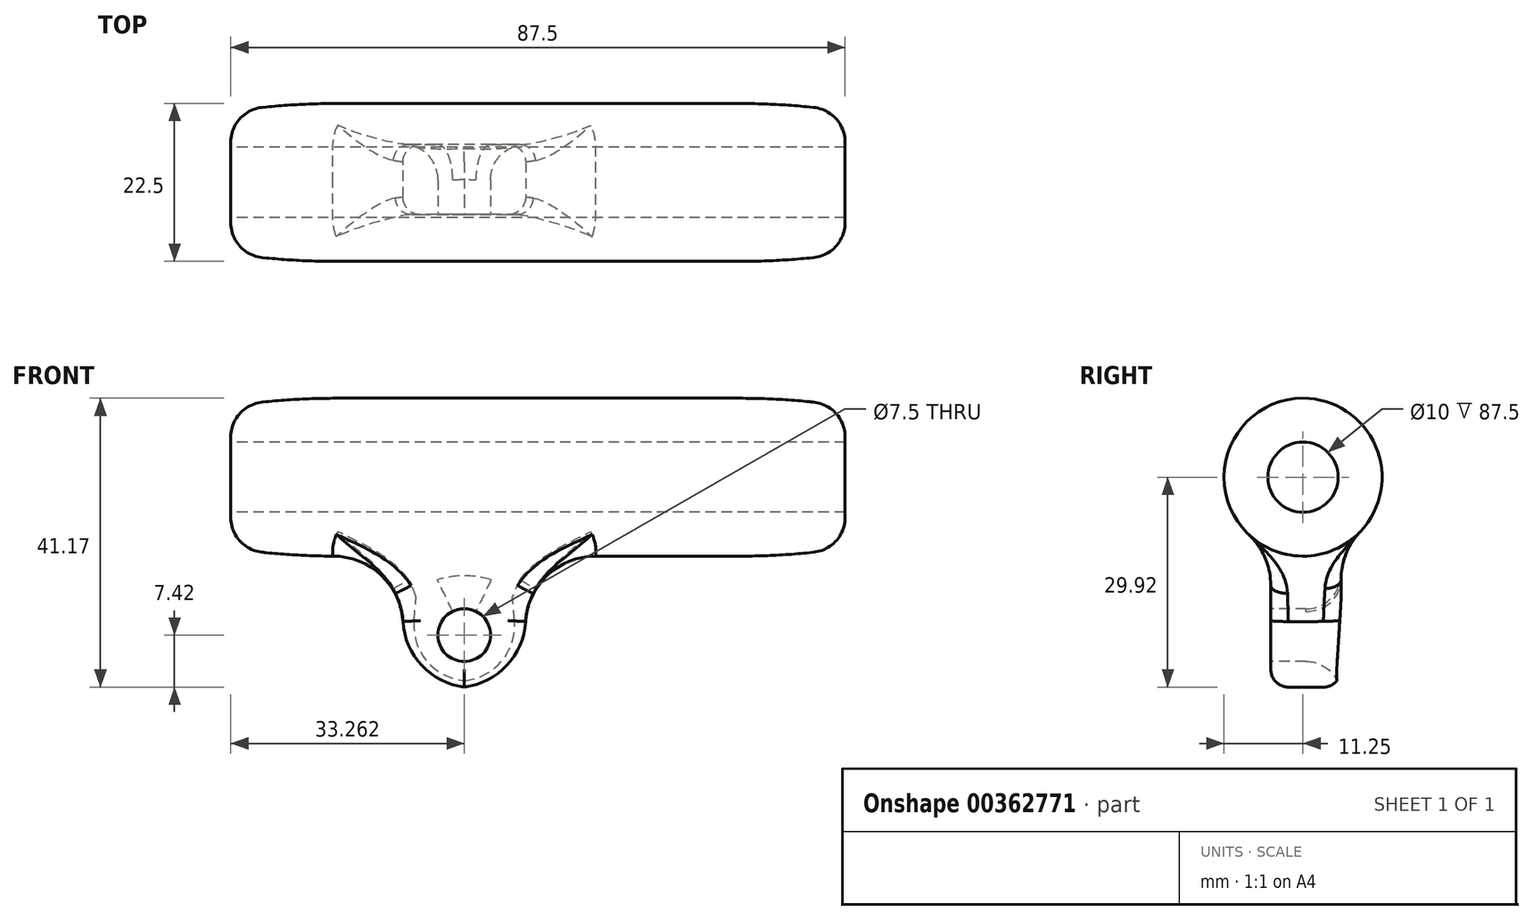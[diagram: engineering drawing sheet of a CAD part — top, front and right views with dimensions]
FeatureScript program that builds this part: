
annotation { "Feature Type Name" : "Feature", "Feature Type Description" : "" }
export const myFeature = defineFeature(function(context is Context, id is Id, definition is map)
    precondition{}
    {
        {
            var Q0;
            Q0=qCreatedBy(makeId("Right.planeOp"),FACE);
            var sketch = newSketch(context, id + "F0", { "sketchPlane" : qUnion([Q0])});
            skCircle(sketch, "E0", {"center": v(0, 0) * mm, "radius": 22.5 * mm});
            skSolve(sketch);
        }
        {
            var Q0;
            Q0=makeQuery(id+"F0.imprint","IMPRINT",FACE,{"disambiguationData":[TD([[makeQuery(id+"F0.imprint","IMPRINT",EDGE,{"derivedFrom":sQuery(id+"F0.wireOp",EDGE,"E0")}),1.0]])]});
            extrude(context, id + "F1", {"entities" : qUnion([Q0]), "depth" : 175 * mm});
        }
        {
            var Q0;
            Q0=qCreatedBy(makeId("Top.planeOp"),FACE);
            var sketch = newSketch(context, id + "F2", { "sketchPlane" : qUnion([Q0])});
            skLineSegment(sketch, "E1.bottom", {"start": v(49.02, -9.18) * mm, "end": v(84.02, -9.18) * mm});
            skLineSegment(sketch, "E1.top", {"start": v(49.02, 10.82) * mm, "end": v(84.02, 10.82) * mm});
            skLineSegment(sketch, "E1.left", {"start": v(49.02, -9.18) * mm, "end": v(49.02, 10.82) * mm});
            skLineSegment(sketch, "E1.right", {"start": v(84.02, -9.18) * mm, "end": v(84.02, 10.82) * mm});
            skSolve(sketch);
        }
        {
            var Q0;
            Q0 = qSketchRegion(id + "F2", true);
            extrude(context, id + "F3", {"entities" : qUnion([Q0]), "operationType" : NewBodyOperationType.ADD, "oppositeDirection" : true, "depth" : 60 * mm});
        }
        {
            var Q0;
            Q0=makeQuery(id+"F1.opExtrude","CAP_FACE",FACE,{"disambiguationData":[OSD([sQuery(id+"F0.wireOp",EDGE,"E0")])],"isStart":true});
            var sketch = newSketch(context, id + "F4", { "sketchPlane" : qUnion([Q0])});
            skCircle(sketch, "E2", {"center": v(0, 0) * mm, "radius": 10 * mm});
            skSolve(sketch);
        }
        {
            var Q0;
            Q0 = qSketchRegion(id + "F4", true);
            extrude(context, id + "F5", {"entities" : qUnion([Q0]), "operationType" : NewBodyOperationType.REMOVE, "endBound" : BoundingType.THROUGH_ALL, "oppositeDirection" : true, "depth" : 25 * mm});
        }
        {
            var Q0;
            Q0=makeQuery(id+"F3.opExtrude","SWEPT_FACE",FACE,{"disambiguationData":[OSD([sQuery(id+"F2.wireOp",EDGE,"E1.bottom")])]});
            var sketch = newSketch(context, id + "F6", { "sketchPlane" : qUnion([Q0])});
            skCircle(sketch, "E3", {"center": v(66.52, -45) * mm, "radius": 7.5 * mm});
            skPoint(sketch, "E3.centerSnap0", {"position": v(66.52, -60) * mm});
            skSolve(sketch);
        }
        {
            var Q0;
            Q0=makeQuery(id+"F6.imprint","IMPRINT",FACE,{"disambiguationData":[TD([[makeQuery(id+"F6.imprint","IMPRINT",EDGE,{"derivedFrom":sQuery(id+"F6.wireOp",EDGE,"E3")}),1.0]])]});
            extrude(context, id + "F7", {"entities" : qUnion([Q0]), "operationType" : NewBodyOperationType.REMOVE, "endBound" : BoundingType.THROUGH_ALL, "oppositeDirection" : true, "depth" : 25 * mm});
        }
        {
            var Q0;
            Q0=makeQuery(id+"F3.opExtrude","CAP_EDGE",EDGE,{"disambiguationData":[OSD([sQuery(id+"F2.wireOp",EDGE,"E1.right")])],"isStart":false});
            var Q1;
            Q1=makeQuery(id+"F3.opExtrude","CAP_EDGE",EDGE,{"disambiguationData":[OSD([sQuery(id+"F2.wireOp",EDGE,"E1.left")])],"isStart":false});
            fillet(context, id + "F8", {"entities" : qUnion([Q0, Q1]), "radius" : 20 * mm, "tangentPropagation" : true, "allowEdgeOverflow" : false});
        }
        {
            var Q0;
            Q0=makeQuery(id+"F3.boolean.opBoolean","INTERSECT",EDGE,{"derivedFrom":[makeQuery(id+"F1.opExtrude","SWEPT_FACE",FACE,{"disambiguationData":[OSD([sQuery(id+"F0.wireOp",EDGE,"E0")])]}),makeQuery(id+"F3.opExtrude","SWEPT_FACE",FACE,{"disambiguationData":[OSD([sQuery(id+"F2.wireOp",EDGE,"E1.right")])]})]});
            fillet(context, id + "F9", {"entities" : qUnion([Q0]), "radius" : 20 * mm, "tangentPropagation" : true, "allowEdgeOverflow" : false});
        }
        {
            var Q0;
            Q0=makeQuery(id+"F3.boolean.opBoolean","INTERSECT",EDGE,{"derivedFrom":[makeQuery(id+"F1.opExtrude","SWEPT_FACE",FACE,{"disambiguationData":[OSD([sQuery(id+"F0.wireOp",EDGE,"E0")])]}),makeQuery(id+"F3.opExtrude","SWEPT_FACE",FACE,{"disambiguationData":[OSD([sQuery(id+"F2.wireOp",EDGE,"E1.left")])]})]});
            fillet(context, id + "F10", {"entities" : qUnion([Q0]), "radius" : 20 * mm, "tangentPropagation" : true, "allowEdgeOverflow" : false});
        }
        {
            var Q0;
            Q0=makeQuery(id+"F3.boolean.opBoolean","INTERSECT",EDGE,{"derivedFrom":[makeQuery(id+"F1.opExtrude","SWEPT_FACE",FACE,{"disambiguationData":[OSD([sQuery(id+"F0.wireOp",EDGE,"E0")])]}),makeQuery(id+"F3.opExtrude","SWEPT_FACE",FACE,{"disambiguationData":[OSD([sQuery(id+"F2.wireOp",EDGE,"E1.top")])]})]});
            var Q1;
            Q1=makeQuery(id+"F3.boolean.opBoolean","INTERSECT",EDGE,{"derivedFrom":[makeQuery(id+"F1.opExtrude","SWEPT_FACE",FACE,{"disambiguationData":[OSD([sQuery(id+"F0.wireOp",EDGE,"E0")])]}),makeQuery(id+"F3.opExtrude","SWEPT_FACE",FACE,{"disambiguationData":[OSD([sQuery(id+"F2.wireOp",EDGE,"E1.bottom")])]})]});
            fillet(context, id + "F11", {"entities" : qUnion([Q0, Q1]), "radius" : 20 * mm, "tangentPropagation" : true, "allowEdgeOverflow" : false});
        }
        {
            var Q0;
            {var subQ0=sQuery(id+"F0.wireOp",EDGE,"E0");Q0=makeQuery(id+"F11.opFillet","BLEND_EDGE",EDGE,{"blendedFrom":[makeQuery(id+"F3.boolean.opBoolean","INTERSECT",EDGE,{"derivedFrom":[makeQuery(id+"F1.opExtrude","SWEPT_FACE",FACE,{"disambiguationData":[OSD([subQ0])]}),makeQuery(id+"F3.opExtrude","SWEPT_FACE",FACE,{"disambiguationData":[OSD([sQuery(id+"F2.wireOp",EDGE,"E1.top")])]})]}),makeQuery(id+"F9.opFillet","BLEND_FACE",FACE,{"disambiguationData":[OSD([subQ0,sQuery(id+"F2.wireOp",EDGE,"E1.right")])]})],"blendedInto":[makeQuery(id+"F9.opFillet","BLEND_FACE",FACE,{"disambiguationData":[OSD([subQ0,sQuery(id+"F2.wireOp",EDGE,"E1.right")])]})]});}
            var Q1;
            {var subQ0=sQuery(id+"F0.wireOp",EDGE,"E0");Q1=makeQuery(id+"F11.opFillet","BLEND_EDGE",EDGE,{"blendedFrom":[makeQuery(id+"F3.boolean.opBoolean","INTERSECT",EDGE,{"derivedFrom":[makeQuery(id+"F1.opExtrude","SWEPT_FACE",FACE,{"disambiguationData":[OSD([subQ0])]}),makeQuery(id+"F3.opExtrude","SWEPT_FACE",FACE,{"disambiguationData":[OSD([sQuery(id+"F2.wireOp",EDGE,"E1.top")])]})]}),makeQuery(id+"F10.opFillet","BLEND_FACE",FACE,{"disambiguationData":[OSD([subQ0,sQuery(id+"F2.wireOp",EDGE,"E1.left")])]})],"blendedInto":[makeQuery(id+"F10.opFillet","BLEND_FACE",FACE,{"disambiguationData":[OSD([subQ0,sQuery(id+"F2.wireOp",EDGE,"E1.left")])]})]});}
            var Q2;
            {var subQ0=sQuery(id+"F0.wireOp",EDGE,"E0");Q2=makeQuery(id+"F11.opFillet","BLEND_EDGE",EDGE,{"blendedFrom":[makeQuery(id+"F3.boolean.opBoolean","INTERSECT",EDGE,{"derivedFrom":[makeQuery(id+"F1.opExtrude","SWEPT_FACE",FACE,{"disambiguationData":[OSD([subQ0])]}),makeQuery(id+"F3.opExtrude","SWEPT_FACE",FACE,{"disambiguationData":[OSD([sQuery(id+"F2.wireOp",EDGE,"E1.bottom")])]})]}),makeQuery(id+"F10.opFillet","BLEND_FACE",FACE,{"disambiguationData":[OSD([subQ0,sQuery(id+"F2.wireOp",EDGE,"E1.left")])]})],"blendedInto":[makeQuery(id+"F10.opFillet","BLEND_FACE",FACE,{"disambiguationData":[OSD([subQ0,sQuery(id+"F2.wireOp",EDGE,"E1.left")])]})]});}
            var Q3;
            {var subQ0=sQuery(id+"F0.wireOp",EDGE,"E0");Q3=makeQuery(id+"F11.opFillet","BLEND_EDGE",EDGE,{"blendedFrom":[makeQuery(id+"F3.boolean.opBoolean","INTERSECT",EDGE,{"derivedFrom":[makeQuery(id+"F1.opExtrude","SWEPT_FACE",FACE,{"disambiguationData":[OSD([subQ0])]}),makeQuery(id+"F3.opExtrude","SWEPT_FACE",FACE,{"disambiguationData":[OSD([sQuery(id+"F2.wireOp",EDGE,"E1.bottom")])]})]}),makeQuery(id+"F9.opFillet","BLEND_FACE",FACE,{"disambiguationData":[OSD([subQ0,sQuery(id+"F2.wireOp",EDGE,"E1.right")])]})],"blendedInto":[makeQuery(id+"F9.opFillet","BLEND_FACE",FACE,{"disambiguationData":[OSD([subQ0,sQuery(id+"F2.wireOp",EDGE,"E1.right")])]})]});}
            fillet(context, id + "F12", {"entities" : qUnion([Q0, Q1, Q2, Q3]), "radius" : 5 * mm, "tangentPropagation" : true, "allowEdgeOverflow" : false});
        }
        {
            var Q0;
            Q0=makeQuery(id+"F1.opExtrude","SWEPT_BODY",BODY,{"disambiguationData":[OSD([sQuery(id+"F0.wireOp",EDGE,"E0")])]});
            var Q1;
            Q1=qCreatedBy(makeId("Origin.pointOp"),VERTEX);
            transform(context, id + "F13", {"entities" : qUnion([Q0]), "transformType" : TransformType.SCALE_UNIFORMLY, "scale" : 0.5, "scalePoint" : qUnion([Q1]), "makeCopy" : false});
        }
        {
            var Q0;
            Q0=makeQuery(id+"F1.opExtrude","CAP_EDGE",EDGE,{"disambiguationData":[OSD([sQuery(id+"F0.wireOp",EDGE,"E0")])],"isStart":false});
            chamfer(context, id + "F14", {"entities" : qUnion([Q0]), "chamferType" : ChamferType.TWO_OFFSETS, "width1" : 1 * mm, "oppositeDirection" : false, "width2" : 10 * mm, "tangentPropagation" : true});
        }
        {
            var Q0;
            Q0=makeQuery(id+"F1.opExtrude","CAP_EDGE",EDGE,{"disambiguationData":[OSD([sQuery(id+"F0.wireOp",EDGE,"E0")])],"isStart":true});
            chamfer(context, id + "F15", {"entities" : qUnion([Q0]), "chamferType" : ChamferType.TWO_OFFSETS, "width1" : 10 * mm, "oppositeDirection" : false, "width2" : 1 * mm, "tangentPropagation" : true});
        }
        {
            var Q0;
            {var subQ0=sQuery(id+"F0.wireOp",EDGE,"E0");Q0=makeQuery(id+"F15.opChamfer","BLEND_EDGE",EDGE,{"blendedFrom":[makeQuery(id+"F1.opExtrude","CAP_EDGE",EDGE,{"disambiguationData":[OSD([subQ0])],"isStart":true}),makeQuery(id+"F1.opExtrude","SWEPT_FACE",FACE,{"disambiguationData":[OSD([subQ0])]})],"blendedInto":[makeQuery(id+"F1.opExtrude","SWEPT_FACE",FACE,{"disambiguationData":[OSD([subQ0])]})]});}
            var Q1;
            {var subQ0=sQuery(id+"F0.wireOp",EDGE,"E0");Q1=makeQuery(id+"F14.opChamfer","BLEND_EDGE",EDGE,{"blendedFrom":[makeQuery(id+"F1.opExtrude","CAP_EDGE",EDGE,{"disambiguationData":[OSD([subQ0])],"isStart":false}),makeQuery(id+"F1.opExtrude","SWEPT_FACE",FACE,{"disambiguationData":[OSD([subQ0])]})],"blendedInto":[makeQuery(id+"F1.opExtrude","SWEPT_FACE",FACE,{"disambiguationData":[OSD([subQ0])]})]});}
            fillet(context, id + "F16", {"entities" : qUnion([Q0, Q1]), "radius" : 100 * mm, "tangentPropagation" : true, "allowEdgeOverflow" : false});
        }
        {
            var Q0;
            {var subQ0=sQuery(id+"F0.wireOp",EDGE,"E0");Q0=makeQuery(id+"F14.opChamfer","BLEND_EDGE",EDGE,{"blendedFrom":[makeQuery(id+"F1.opExtrude","CAP_EDGE",EDGE,{"disambiguationData":[OSD([subQ0])],"isStart":false}),makeQuery(id+"F1.opExtrude","CAP_FACE",FACE,{"disambiguationData":[OSD([subQ0])],"isStart":false})],"blendedInto":[makeQuery(id+"F1.opExtrude","CAP_FACE",FACE,{"disambiguationData":[OSD([subQ0])],"isStart":false})]});}
            var Q1;
            {var subQ0=sQuery(id+"F0.wireOp",EDGE,"E0");Q1=makeQuery(id+"F15.opChamfer","BLEND_EDGE",EDGE,{"blendedFrom":[makeQuery(id+"F1.opExtrude","CAP_EDGE",EDGE,{"disambiguationData":[OSD([subQ0])],"isStart":true}),makeQuery(id+"F1.opExtrude","CAP_FACE",FACE,{"disambiguationData":[OSD([subQ0])],"isStart":true})],"blendedInto":[makeQuery(id+"F1.opExtrude","CAP_FACE",FACE,{"disambiguationData":[OSD([subQ0])],"isStart":true})]});}
            var Q2;
            Q2=makeQuery(id+"F7.boolean.opBoolean","INTERSECT",EDGE,{"derivedFrom":[makeQuery(id+"F3.opExtrude","SWEPT_FACE",FACE,{"disambiguationData":[OSD([sQuery(id+"F2.wireOp",EDGE,"E1.top")])]}),makeQuery(id+"F7.opExtrude","SWEPT_FACE",FACE,{"disambiguationData":[OSD([sQuery(id+"F6.wireOp",EDGE,"E3")])]})]});
            var Q3;
            Q3=makeQuery(id+"F7.boolean.opBoolean","COPY",EDGE,{"derivedFrom":makeQuery(id+"F7.opExtrude","CAP_EDGE",EDGE,{"disambiguationData":[OSD([sQuery(id+"F6.wireOp",EDGE,"E3")])],"isStart":true})});
            fillet(context, id + "F17", {"entities" : qUnion([Q0, Q1, Q2, Q3]), "radius" : 5 * mm, "tangentPropagation" : true, "allowEdgeOverflow" : false});
        }
    });
